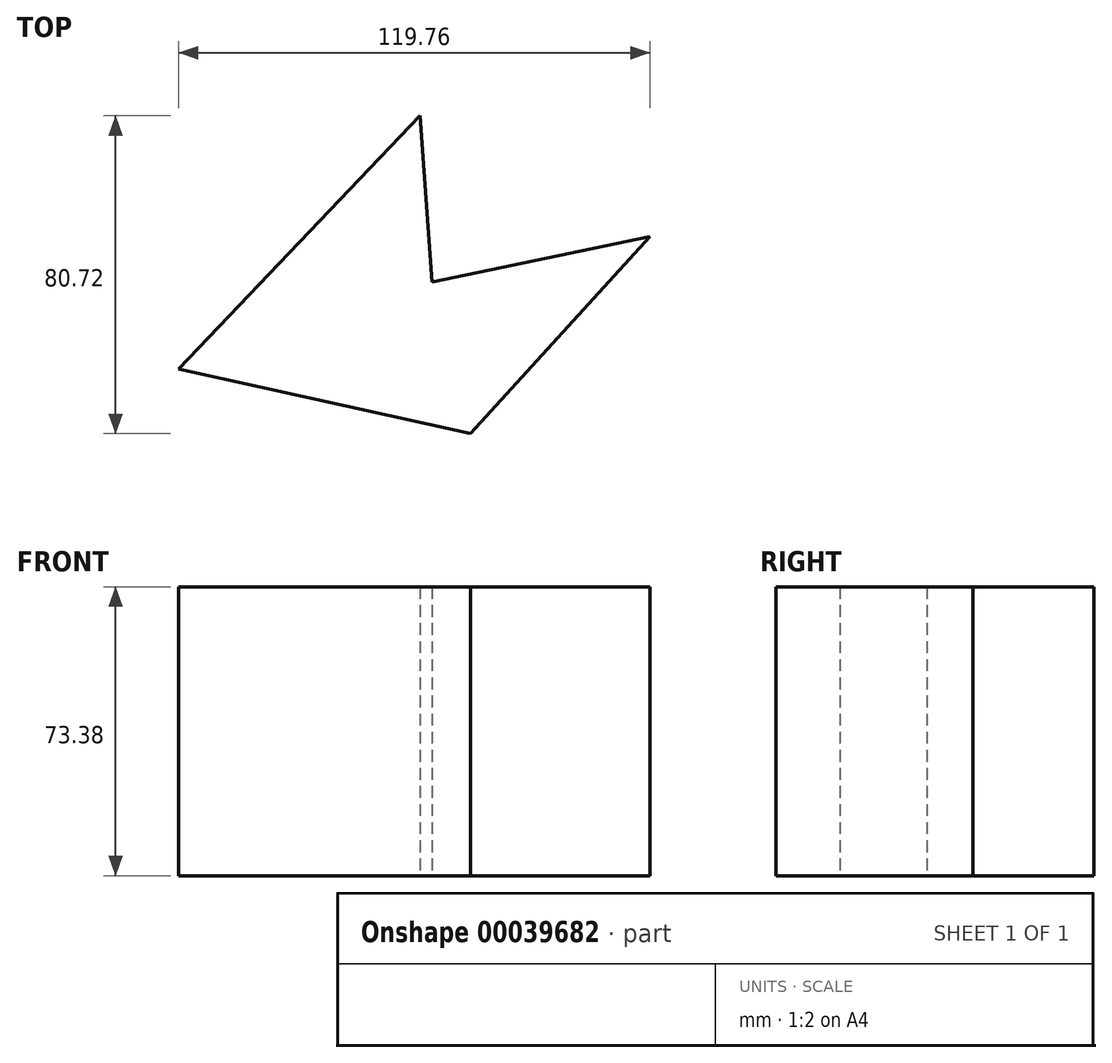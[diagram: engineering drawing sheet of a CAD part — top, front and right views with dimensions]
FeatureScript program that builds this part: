
annotation { "Feature Type Name" : "Feature", "Feature Type Description" : "" }
export const myFeature = defineFeature(function(context is Context, id is Id, definition is map)
    precondition{}
    {
        {
            var Q0;
            Q0=qCreatedBy(makeId("Top.planeOp"),FACE);
            var sketch = newSketch(context, id + "F0", { "sketchPlane" : qUnion([Q0])});
            skLineSegment(sketch, "E0", {"start": v(-38.49, -34.77) * mm, "end": v(22.87, 29.64) * mm});
            skLineSegment(sketch, "E1", {"start": v(-38.49, -34.77) * mm, "end": v(35.68, -51.08) * mm});
            skLineSegment(sketch, "E2", {"start": v(35.68, -51.08) * mm, "end": v(82.23, 0) * mm});
            skLineSegment(sketch, "E3", {"start": v(82.66, -0.77) * mm, "end": v(25.9, -12.67) * mm});
            skLineSegment(sketch, "E4", {"start": v(25.9, -12.67) * mm, "end": v(22.87, 29.64) * mm});
            skSolve(sketch);
        }
        {
            var Q0;
            Q0=makeQuery(id+"F0.imprint","IMPRINT",FACE,{"disambiguationData":[TD([[makeQuery(id+"F0.imprint","IMPRINT",EDGE,{"derivedFrom":sQuery(id+"F0.wireOp",EDGE,"E0")}),-1.0]])]});
            extrude(context, id + "F1", {"entities" : qUnion([Q0]), "endBound" : BoundingType.SYMMETRIC, "depth" : 73.38 * mm});
        }
    });
